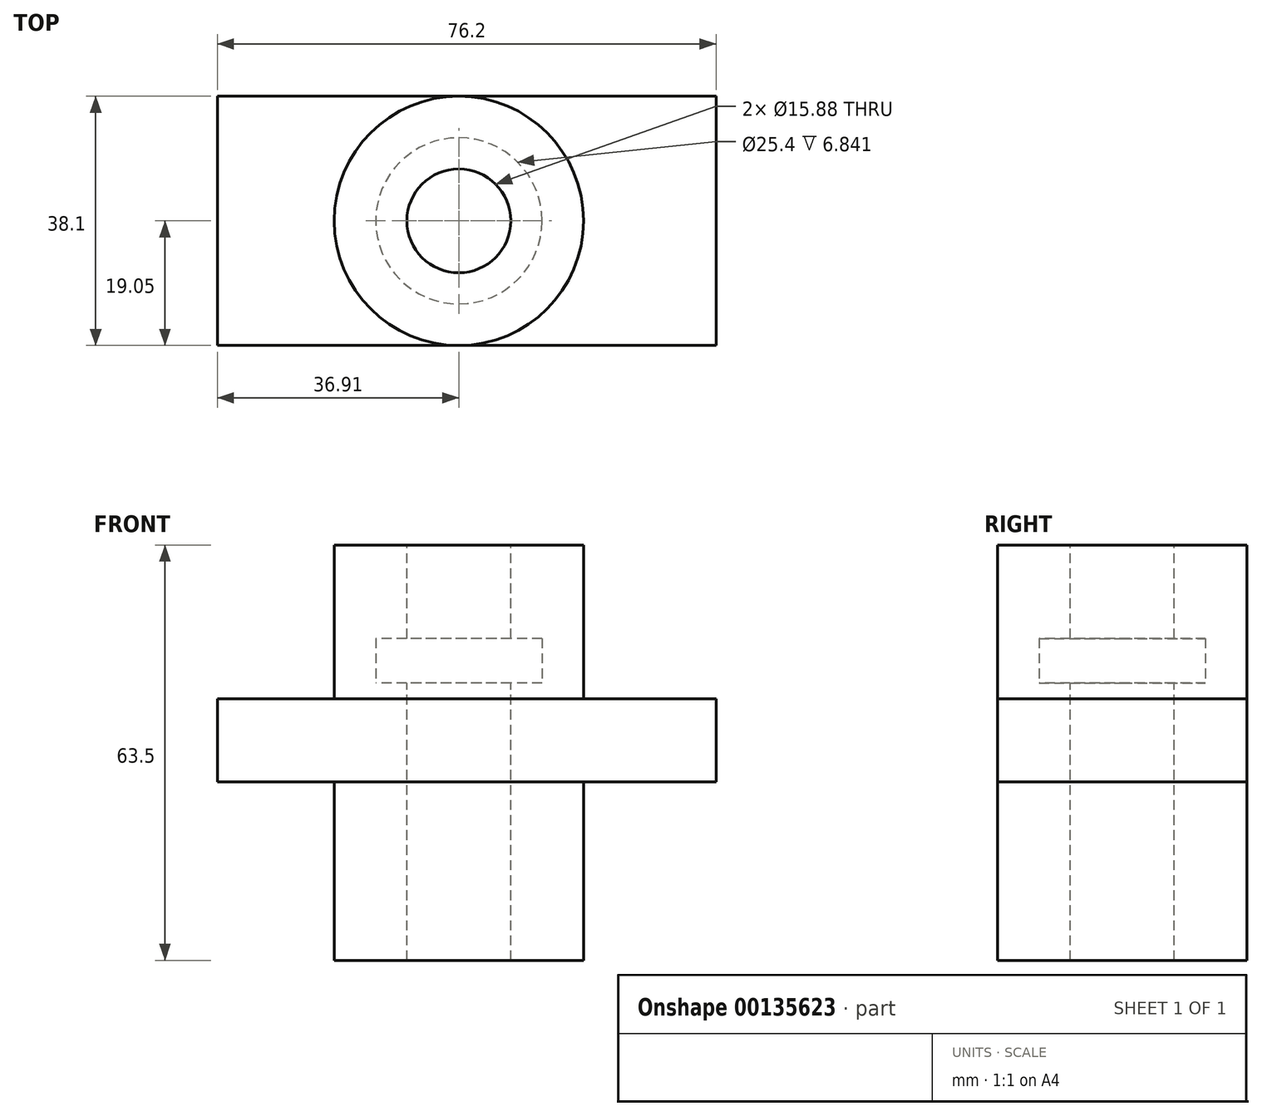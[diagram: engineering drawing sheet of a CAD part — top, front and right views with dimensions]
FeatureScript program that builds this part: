
annotation { "Feature Type Name" : "Feature", "Feature Type Description" : "" }
export const myFeature = defineFeature(function(context is Context, id is Id, definition is map)
    precondition{}
    {
        {
            var Q0;
            Q0=qCreatedBy(makeId("Front.planeOp"),FACE);
            var sketch = newSketch(context, id + "F0", { "sketchPlane" : qUnion([Q0])});
            skLineSegment(sketch, "E0.bottom", {"start": v(-36.9, 8.25) * mm, "end": v(39.3, 8.25) * mm});
            skLineSegment(sketch, "E0.top", {"start": v(-36.9, 20.95) * mm, "end": v(39.3, 20.95) * mm});
            skLineSegment(sketch, "E0.left", {"start": v(-36.9, 8.25) * mm, "end": v(-36.9, 20.95) * mm});
            skLineSegment(sketch, "E0.right", {"start": v(39.3, 8.25) * mm, "end": v(39.3, 20.95) * mm});
            skSolve(sketch);
        }
        {
            var Q0;
            Q0 = qSketchRegion(id + "F0", true);
            extrude(context, id + "F1", {"entities" : qUnion([Q0]), "endBound" : BoundingType.SYMMETRIC, "depth" : 38.1 * mm});
        }
        {
            var Q0;
            Q0=qCreatedBy(makeId("Top.planeOp"),FACE);
            var sketch = newSketch(context, id + "F2", { "sketchPlane" : qUnion([Q0])});
            skCircle(sketch, "E1", {"center": v(0, 0) * mm, "radius": 19.05 * mm});
            skSolve(sketch);
        }
        {
            var Q0;
            Q0 = qSketchRegion(id + "F2", true);
            var Q1;
            Q1=makeQuery(id+"F1.opExtrude","SWEPT_FACE",FACE,{"disambiguationData":[OSD([sQuery(id+"F0.wireOp",EDGE,"E0.top")])]});
            var Q2;
            Q2=makeQuery(id+"F1.opExtrude","SWEPT_BODY",BODY,{"disambiguationData":[OSD([sQuery(id+"F0.wireOp",EDGE,"E0.bottom"),sQuery(id+"F0.wireOp",EDGE,"E0.top"),sQuery(id+"F0.wireOp",EDGE,"E0.left"),sQuery(id+"F0.wireOp",EDGE,"E0.right")])]});
            var Q3;
            Q3=makeQuery(id+"F1.opExtrude","SWEPT_FACE",FACE,{"disambiguationData":[OSD([sQuery(id+"F0.wireOp",EDGE,"E0.bottom")])]});
            extrude(context, id + "F3", {"entities" : qUnion([Q0]), "operationType" : NewBodyOperationType.ADD, "oppositeDirection" : true, "endBoundEntityFace" : qUnion([Q1]), "endBoundEntityBody" : qUnion([Q2]), "depth" : 19.05 * mm, "hasSecondDirection" : true, "secondDirectionBound" : SecondDirectionBoundingType.UP_TO_SURFACE, "secondDirectionOppositeDirection" : false, "secondDirectionBoundEntityFace" : qUnion([Q3]), "secondDirectionDepth" : 25.4 * mm});
        }
        {
            var Q0;
            Q0 = qSketchRegion(id + "F2", true);
            var Q1;
            Q1=makeQuery(id+"F1.opExtrude","SWEPT_FACE",FACE,{"disambiguationData":[OSD([sQuery(id+"F0.wireOp",EDGE,"E0.top")])]});
            extrude(context, id + "F4", {"entities" : qUnion([Q0]), "operationType" : NewBodyOperationType.ADD, "depth" : 44.45 * mm, "hasSecondDirection" : true, "secondDirectionBound" : SecondDirectionBoundingType.UP_TO_SURFACE, "secondDirectionOppositeDirection" : false, "secondDirectionBoundEntityFace" : qUnion([Q1]), "secondDirectionDepth" : 25.4 * mm});
        }
        {
            var Q0;
            Q0=qCreatedBy(makeId("Top.planeOp"),FACE);
            var sketch = newSketch(context, id + "F5", { "sketchPlane" : qUnion([Q0])});
            skCircle(sketch, "E2", {"center": v(0, 0) * mm, "radius": 7.94 * mm});
            skSolve(sketch);
        }
        {
            var Q0;
            Q0 = qSketchRegion(id + "F5", true);
            extrude(context, id + "F6", {"entities" : qUnion([Q0]), "operationType" : NewBodyOperationType.REMOVE, "endBound" : BoundingType.SYMMETRIC, "oppositeDirection" : true, "depth" : 203.2 * mm});
        }
        {
            var Q0;
            Q0=qCreatedBy(makeId("Top.planeOp"),FACE);
            var sketch = newSketch(context, id + "F7", { "sketchPlane" : qUnion([Q0])});
            skCircle(sketch, "E3", {"center": v(0, 0) * mm, "radius": 12.7 * mm});
            skSolve(sketch);
        }
        {
            var Q0;
            Q0 = qSketchRegion(id + "F7", true);
            extrude(context, id + "F8", {"entities" : qUnion([Q0]), "operationType" : NewBodyOperationType.REMOVE, "depth" : 30.17 * mm, "hasSecondDirection" : true, "secondDirectionOppositeDirection" : false, "secondDirectionDepth" : 23.33 * mm});
        }
    });
